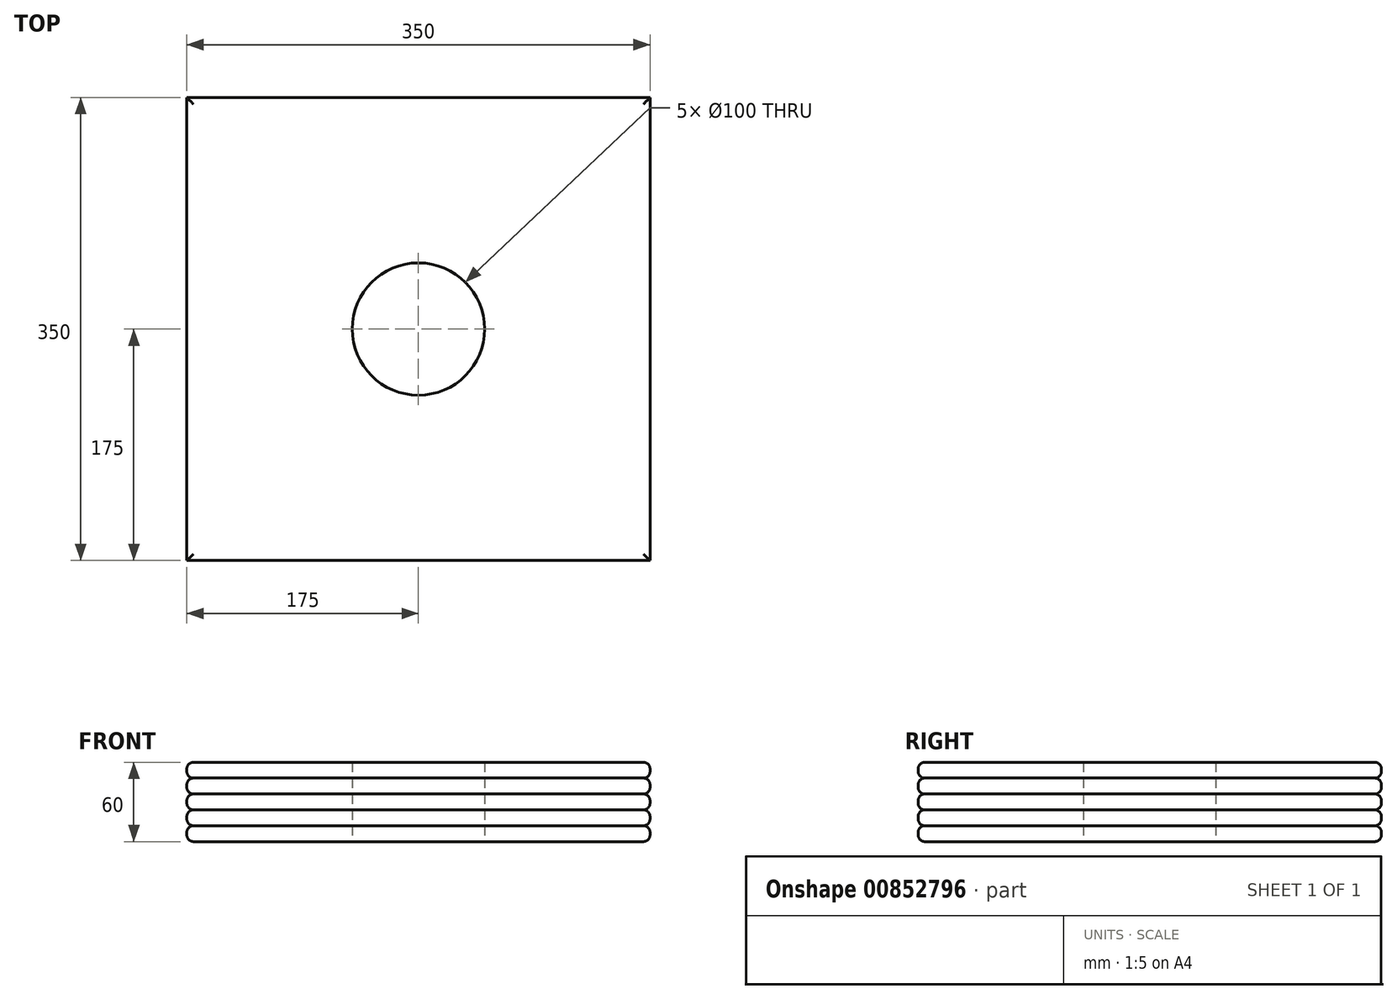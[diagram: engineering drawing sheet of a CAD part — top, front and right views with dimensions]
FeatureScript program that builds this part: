
annotation { "Feature Type Name" : "Feature", "Feature Type Description" : "" }
export const myFeature = defineFeature(function(context is Context, id is Id, definition is map)
    precondition{}
    {
        {
            var Q0;
            Q0=qCreatedBy(makeId("Top.planeOp"),FACE);
            var sketch = newSketch(context, id + "F0", { "sketchPlane" : qUnion([Q0])});
            skLineSegment(sketch, "E0.bottom", {"start": v(-175, 175) * mm, "end": v(175, 175) * mm});
            skLineSegment(sketch, "E0.top", {"start": v(-175, -175) * mm, "end": v(175, -175) * mm});
            skLineSegment(sketch, "E0.left", {"start": v(-175, 175) * mm, "end": v(-175, -175) * mm});
            skLineSegment(sketch, "E0.right", {"start": v(175, 175) * mm, "end": v(175, -175) * mm});
            skPoint(sketch, "E0.middle", {"position": v(0, 0) * mm});
            skCircle(sketch, "E1", {"center": v(0, 0) * mm, "radius": 50 * mm});
            skSolve(sketch);
        }
        {
            var Q0;
            Q0 = qSketchRegion(id + "F0", true);
            extrude(context, id + "F1", {"entities" : qUnion([Q0]), "depth" : 12 * mm, "offsetDistance" : 25 * mm});
        }
        {
            var Q0;
            Q0=makeQuery(id+"F1.opExtrude","CAP_EDGE",EDGE,{"disambiguationData":[OSD([sQuery(id+"F0.wireOp",EDGE,"E0.top")])],"isStart":true});
            var Q1;
            Q1=makeQuery(id+"F1.opExtrude","CAP_EDGE",EDGE,{"disambiguationData":[OSD([sQuery(id+"F0.wireOp",EDGE,"E0.right")])],"isStart":true});
            var Q2;
            Q2=makeQuery(id+"F1.opExtrude","CAP_EDGE",EDGE,{"disambiguationData":[OSD([sQuery(id+"F0.wireOp",EDGE,"E0.bottom")])],"isStart":true});
            var Q3;
            Q3=makeQuery(id+"F1.opExtrude","CAP_EDGE",EDGE,{"disambiguationData":[OSD([sQuery(id+"F0.wireOp",EDGE,"E0.left")])],"isStart":true});
            var Q4;
            Q4=makeQuery(id+"F1.opExtrude","CAP_EDGE",EDGE,{"disambiguationData":[OSD([sQuery(id+"F0.wireOp",EDGE,"E0.left")])],"isStart":false});
            var Q5;
            Q5=makeQuery(id+"F1.opExtrude","CAP_EDGE",EDGE,{"disambiguationData":[OSD([sQuery(id+"F0.wireOp",EDGE,"E0.top")])],"isStart":false});
            var Q6;
            Q6=makeQuery(id+"F1.opExtrude","CAP_EDGE",EDGE,{"disambiguationData":[OSD([sQuery(id+"F0.wireOp",EDGE,"E0.right")])],"isStart":false});
            var Q7;
            Q7=makeQuery(id+"F1.opExtrude","CAP_EDGE",EDGE,{"disambiguationData":[OSD([sQuery(id+"F0.wireOp",EDGE,"E0.bottom")])],"isStart":false});
            fillet(context, id + "F2", {"entities" : qUnion([Q0, Q1, Q2, Q3, Q4, Q5, Q6, Q7]), "radius" : 5 * mm, "tangentPropagation" : true, "allowEdgeOverflow" : false});
        }
        {
            var Q0;
            Q0=makeQuery(id+"F1.opExtrude","SWEPT_BODY",BODY,{"disambiguationData":[OSD([sQuery(id+"F0.wireOp",EDGE,"E0.bottom"),sQuery(id+"F0.wireOp",EDGE,"E0.top"),sQuery(id+"F0.wireOp",EDGE,"E0.left"),sQuery(id+"F0.wireOp",EDGE,"E0.right"),sQuery(id+"F0.wireOp",EDGE,"E1")])]});
            transform(context, id + "F3", {"entities" : qUnion([Q0]), "transformType" : TransformType.TRANSLATION_3D, "dx" : 0 * mm, "dy" : 0 * mm, "dz" : 12 * mm, "makeCopy" : true});
        }
        {
            var Q0;
            Q0=makeQuery(id+"F3.opPattern","COPY",BODY,{"derivedFrom":makeQuery(id+"F1.opExtrude","SWEPT_BODY",BODY,{"disambiguationData":[OSD([sQuery(id+"F0.wireOp",EDGE,"E0.bottom"),sQuery(id+"F0.wireOp",EDGE,"E0.top"),sQuery(id+"F0.wireOp",EDGE,"E0.left"),sQuery(id+"F0.wireOp",EDGE,"E0.right"),sQuery(id+"F0.wireOp",EDGE,"E1")])]}),"instanceName":"1"});
            transform(context, id + "F4", {"entities" : qUnion([Q0]), "transformType" : TransformType.TRANSLATION_3D, "dx" : 0 * mm, "dy" : 0 * mm, "dz" : 12 * mm, "makeCopy" : true});
        }
        {
            var Q0;
            Q0=makeQuery(id+"F4.opPattern","COPY",BODY,{"derivedFrom":makeQuery(id+"F3.opPattern","COPY",BODY,{"derivedFrom":makeQuery(id+"F1.opExtrude","SWEPT_BODY",BODY,{"disambiguationData":[OSD([sQuery(id+"F0.wireOp",EDGE,"E0.bottom"),sQuery(id+"F0.wireOp",EDGE,"E0.top"),sQuery(id+"F0.wireOp",EDGE,"E0.left"),sQuery(id+"F0.wireOp",EDGE,"E0.right"),sQuery(id+"F0.wireOp",EDGE,"E1")])]}),"instanceName":"1"}),"instanceName":"1"});
            transform(context, id + "F5", {"entities" : qUnion([Q0]), "transformType" : TransformType.TRANSLATION_3D, "dx" : 0 * mm, "dy" : 0 * mm, "dz" : 12 * mm, "makeCopy" : true});
        }
        {
            var Q0;
            Q0=makeQuery(id+"F5.opPattern","COPY",BODY,{"derivedFrom":makeQuery(id+"F4.opPattern","COPY",BODY,{"derivedFrom":makeQuery(id+"F3.opPattern","COPY",BODY,{"derivedFrom":makeQuery(id+"F1.opExtrude","SWEPT_BODY",BODY,{"disambiguationData":[OSD([sQuery(id+"F0.wireOp",EDGE,"E0.bottom"),sQuery(id+"F0.wireOp",EDGE,"E0.top"),sQuery(id+"F0.wireOp",EDGE,"E0.left"),sQuery(id+"F0.wireOp",EDGE,"E0.right"),sQuery(id+"F0.wireOp",EDGE,"E1")])]}),"instanceName":"1"}),"instanceName":"1"}),"instanceName":"1"});
            transform(context, id + "F6", {"entities" : qUnion([Q0]), "transformType" : TransformType.TRANSLATION_3D, "dx" : 0 * mm, "dy" : 0 * mm, "dz" : 12 * mm, "makeCopy" : true});
        }
    });
